# Revit family: FU_Table_Sandler_REUNION 1281
name_source: partatom
category: Furniture
units: mm (PartAtom-declared; Revit-internal decimal feet)

## family parameters
Always vertical = No
Cut with Voids When Loaded = No
OmniClass Number = 23.21.23.15.17
Room Calculation Point = No
Shared = No
Work Plane-Based = Yes

## types (2) — shared parameters
BIMobject category = Table
BIMobject category code = furniture-table
BIMobject main category = Furniture
BIMobject main category code = furniture
Brand url = https://www.sandlerseating.com
Description = Table
Edition number = 1
IFC Classification = Furnishing Element
Manufacturer = Sandler
Manufacturer country = USA
Manufacturer name = Sandler
Masterformat 2014 Code = 12 48 43.13
Masterformat 2014 Description = Table Mats
OmniClass Code = 23-21 23 15 17
P Depth = 590 mm  [stored 1.9357 ft]
Product Guid = ??
Product SKU = ??
Product data url = https://www.sandlerseating.com
Product family = Furniture
Product group = Table
Product url = https://www.sandlerseating.com
QR code = https://www.sandlerseating.com
Uniformat II Description = Movable Furnishings
X-Offset = 470 mm  [stored 1.54199 ft]
Z-Offset = 355 mm
zero-valued in all types: Default Elevation

## per-type parameters (varying)
| type | Height | Model | Product name |
| REUNION 1281A | 960 mm  [stored 3.14961 ft] | REUNION 1281A | REUNION 1281A |
| REUNION 1280B | 810 mm | REUNION 1281B | REUNION 1281B |

note: [stored X ft] marks values corroborated as IEEE doubles in the binary element streams (Revit-internal decimal feet)

## geometry (parser evidence)
native form markers: Sweep x6
no freeform markers — native parametric forms only
